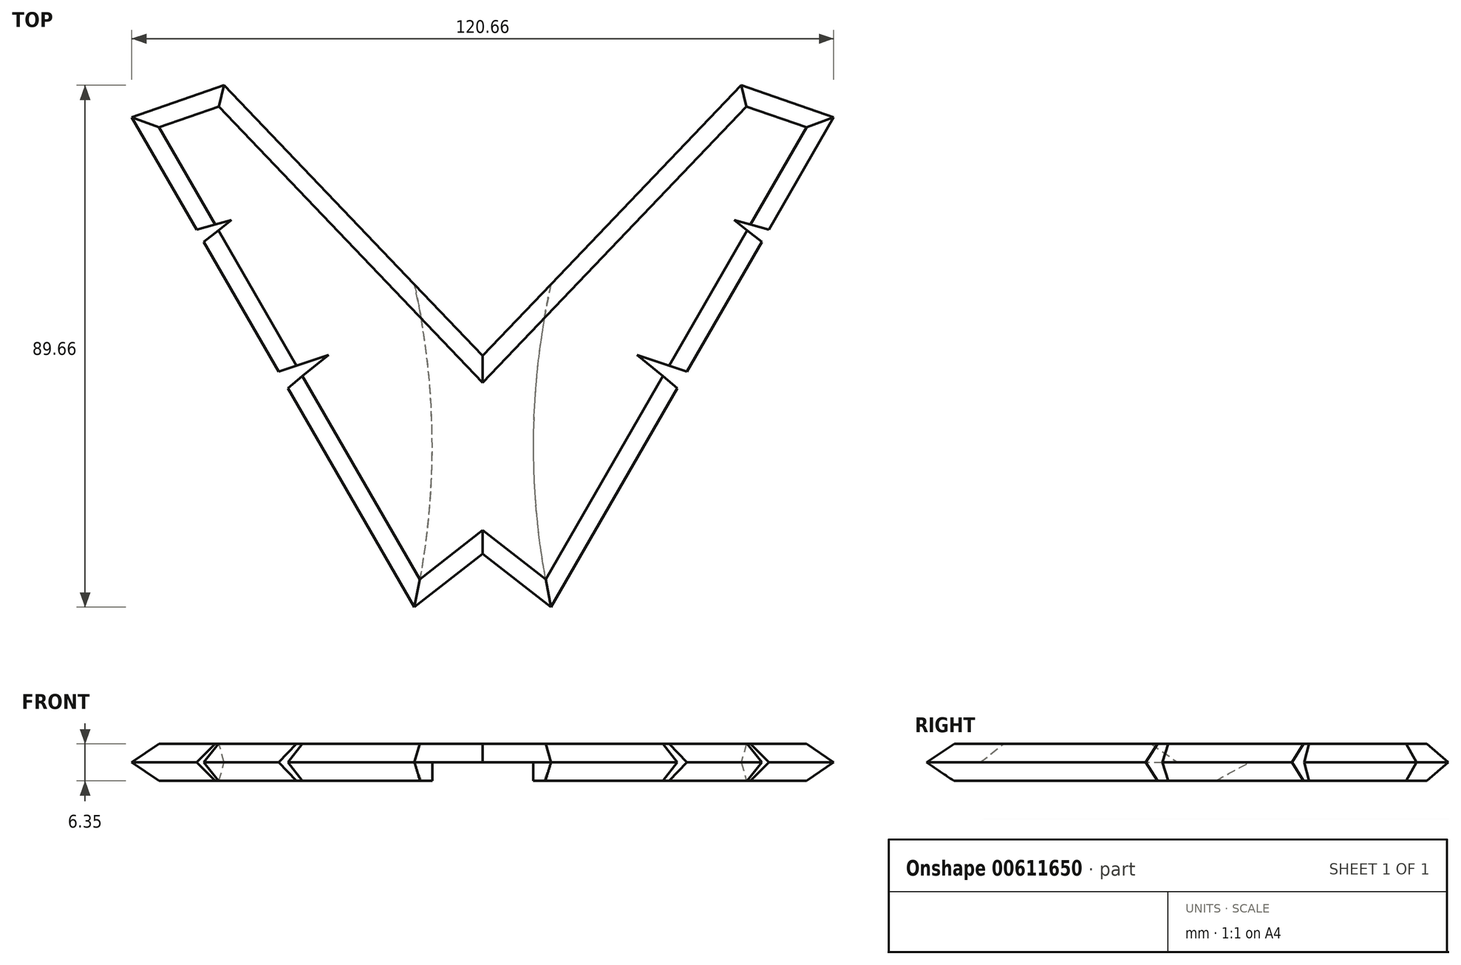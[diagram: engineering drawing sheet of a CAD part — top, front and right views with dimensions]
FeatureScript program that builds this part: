
annotation { "Feature Type Name" : "Feature", "Feature Type Description" : "" }
export const myFeature = defineFeature(function(context is Context, id is Id, definition is map)
    precondition{}
    {
        {
            var Q0;
            Q0=qCreatedBy(makeId("Top.planeOp"),FACE);
            var sketch = newSketch(context, id + "F0", { "sketchPlane" : qUnion([Q0])});
            skLineSegment(sketch, "E0", {"start": v(0, 0) * mm, "end": v(-11.74, 20.33) * mm});
            skLineSegment(sketch, "E1", {"start": v(-63.5, 109.99) * mm, "end": v(63.5, 109.99) * mm});
            skLineSegment(sketch, "E2", {"start": v(63.5, 109.99) * mm, "end": v(0, 0) * mm});
            skLineSegment(sketch, "E3", {"start": v(0, 0) * mm, "end": v(0, 19.44) * mm});
            skLineSegment(sketch, "E4", {"start": v(-60.33, 104.49) * mm, "end": v(-44.45, 109.99) * mm});
            skLineSegment(sketch, "E5.MirrorCS", {"start": v(60.33, 104.49) * mm, "end": v(44.45, 109.99) * mm});
            skLineSegment(sketch, "E6", {"start": v(-44.45, 109.99) * mm, "end": v(0, 63.5) * mm});
            skLineSegment(sketch, "E7", {"start": v(0, 63.5) * mm, "end": v(44.45, 109.99) * mm});
            skPoint(sketch, "E8", {"position": v(-11.74, 20.33) * mm});
            skPoint(sketch, "E9.MirrorP", {"position": v(11.74, 20.33) * mm});
            skLineSegment(sketch, "E10.MirrorCS", {"start": v(11.74, 20.33) * mm, "end": v(0, 29.52) * mm});
            skLineSegment(sketch, "E11.MirrorCS", {"start": v(0, 29.52) * mm, "end": v(-11.74, 20.33) * mm});
            skLineSegment(sketch, "E12", {"start": v(-49.19, 85.2) * mm, "end": v(-43.22, 86.8) * mm});
            skLineSegment(sketch, "E13", {"start": v(-43.22, 86.8) * mm, "end": v(-47.97, 83.1) * mm});
            skLineSegment(sketch, "E14", {"start": v(-35.1, 60.8) * mm, "end": v(-26.52, 63.68) * mm});
            skLineSegment(sketch, "E15", {"start": v(-26.52, 63.68) * mm, "end": v(-33.47, 57.97) * mm});
            skLineSegment(sketch, "E16.trimOffspring", {"start": v(-21.1, 36.55) * mm, "end": v(-33.47, 57.97) * mm});
            skLineSegment(sketch, "E17.trimOffspring", {"start": v(-35.1, 60.8) * mm, "end": v(-47.97, 83.1) * mm});
            skLineSegment(sketch, "E18.trimOffspring", {"start": v(-49.19, 85.2) * mm, "end": v(-63.5, 109.99) * mm});
            skLineSegment(sketch, "E19.MirrorCS", {"start": v(26.52, 63.68) * mm, "end": v(33.47, 57.97) * mm});
            skLineSegment(sketch, "E20.MirrorCS", {"start": v(35.1, 60.8) * mm, "end": v(26.52, 63.68) * mm});
            skLineSegment(sketch, "E21.MirrorCS", {"start": v(43.22, 86.8) * mm, "end": v(47.97, 83.1) * mm});
            skLineSegment(sketch, "E22.MirrorCS", {"start": v(49.19, 85.2) * mm, "end": v(43.22, 86.8) * mm});
            skLineSegment(sketch, "E23", {"start": v(-21.1, 36.55) * mm, "end": v(-11.74, 20.33) * mm});
            skSolve(sketch);
        }
        {
            var Q0;
            {var subQ3=sQuery(id+"F0.wireOp",EDGE,"E4");Q0=makeQuery(id+"F0.imprint","IMPRINT",FACE,{"disambiguationData":[TD([[makeQuery(id+"F0.imprint","IMPRINT",EDGE,{"derivedFrom":subQ3}),-1.0]])]});}
            extrude(context, id + "F1", {"entities" : qUnion([Q0]), "depth" : 6.35 * mm, "offsetDistance" : 25.4 * mm});
        }
        {
            var Q0;
            Q0=makeQuery(id+"F1.opExtrude","CAP_FACE",FACE,{"disambiguationData":[OSD([sQuery(id+"F0.wireOp",EDGE,"E2"),sQuery(id+"F0.wireOp",EDGE,"E4"),sQuery(id+"F0.wireOp",EDGE,"E5.MirrorCS"),sQuery(id+"F0.wireOp",EDGE,"E6"),sQuery(id+"F0.wireOp",EDGE,"E7"),sQuery(id+"F0.wireOp",EDGE,"E10.MirrorCS"),sQuery(id+"F0.wireOp",EDGE,"E11.MirrorCS"),sQuery(id+"F0.wireOp",EDGE,"E12"),sQuery(id+"F0.wireOp",EDGE,"E13"),sQuery(id+"F0.wireOp",EDGE,"E14"),sQuery(id+"F0.wireOp",EDGE,"E15"),sQuery(id+"F0.wireOp",EDGE,"E16.trimOffspring"),sQuery(id+"F0.wireOp",EDGE,"E17.trimOffspring"),sQuery(id+"F0.wireOp",EDGE,"E18.trimOffspring"),sQuery(id+"F0.wireOp",EDGE,"E19.MirrorCS"),sQuery(id+"F0.wireOp",EDGE,"E20.MirrorCS"),sQuery(id+"F0.wireOp",EDGE,"E21.MirrorCS"),sQuery(id+"F0.wireOp",EDGE,"E22.MirrorCS"),sQuery(id+"F0.wireOp",EDGE,"E23")])],"isStart":true});
            var sketch = newSketch(context, id + "F2", { "sketchPlane" : qUnion([Q0])});
            skPoint(sketch, "E24", {"position": v(11.74, -75.77) * mm});
            skPoint(sketch, "E25", {"position": v(-11.74, -75.77) * mm});
            skArc(sketch, "E26", {"start": v(11.74, -20.33) * mm, "mid": v(8.67, -48.05) * mm, "end": v(11.74, -75.77) * mm});
            skArc(sketch, "E27.MirrorCS", {"start": v(-11.74, -20.33) * mm, "mid": v(-8.67, -48.05) * mm, "end": v(-11.74, -75.77) * mm});
            skLineSegment(sketch, "E28", {"start": v(11.74, -75.77) * mm, "end": v(-11.74, -75.77) * mm});
            skLineSegment(sketch, "E29", {"start": v(-11.74, -20.33) * mm, "end": v(11.74, -20.33) * mm});
            skSolve(sketch);
        }
        {
            var Q0;
            {var subQ5=sQuery(id+"F2.wireOp",EDGE,"E26");Q0=makeQuery(id+"F2.imprint","IMPRINT",FACE,{"disambiguationData":[TD([[makeQuery(id+"F2.imprint","IMPRINT",EDGE,{"derivedFrom":subQ5}),-1.0]])]});}
            var Q1;
            {var subQ0=sQuery(id+"F2.wireOp",EDGE,"E28");Q1=makeQuery(id+"F2.imprint","IMPRINT",FACE,{"disambiguationData":[TD([[makeQuery(id+"F2.imprint","IMPRINT",EDGE,{"derivedFrom":subQ0}),-1.0]])]});}
            var Q2;
            Q2=makeQuery(id+"F2.imprint","IMPRINT",FACE,{"disambiguationData":[TD([[makeQuery(id+"F2.imprint","IMPRINT",EDGE,{"derivedFrom":sQuery(id+"F2.wireOp",EDGE,"E29")}),-1.0]])]});
            extrude(context, id + "F3", {"entities" : qUnion([Q0, Q1, Q2]), "operationType" : NewBodyOperationType.REMOVE, "oppositeDirection" : true, "depth" : 3.17 * mm, "offsetDistance" : 25.4 * mm});
        }
        {
            var Q0;
            {var subQ0=sQuery(id+"F0.wireOp",EDGE,"E2");Q0=makeQuery(id+"F1.opExtrude","CAP_EDGE",EDGE,{"disambiguationData":[OSD([subQ0]),TDD([makeQuery(id+"F0.imprint","IMPRINT",EDGE,{"disambiguationData":[TD([[makeQuery(id+"F0.imprint","INTERSECT",VERTEX,{"derivedFrom":[subQ0,sQuery(id+"F0.wireOp",EDGE,"E10.MirrorCS")]}),1.0]])],"derivedFrom":subQ0})])],"isStart":false});}
            var Q1;
            {var subQ0=sQuery(id+"F0.wireOp",EDGE,"E2");Q1=makeQuery(id+"F1.opExtrude","CAP_EDGE",EDGE,{"disambiguationData":[OSD([subQ0]),TDD([makeQuery(id+"F0.imprint","IMPRINT",EDGE,{"disambiguationData":[TD([[makeQuery(id+"F0.imprint","INTERSECT",VERTEX,{"derivedFrom":[subQ0,sQuery(id+"F0.wireOp",EDGE,"E10.MirrorCS")]}),1.0]])],"derivedFrom":subQ0})])],"isStart":true});}
            var Q2;
            {var subQ0=sQuery(id+"F0.wireOp",EDGE,"E2");Q2=makeQuery(id+"F1.opExtrude","CAP_EDGE",EDGE,{"disambiguationData":[OSD([subQ0]),TDD([makeQuery(id+"F0.imprint","IMPRINT",EDGE,{"disambiguationData":[TD([[makeQuery(id+"F0.imprint","INTERSECT",VERTEX,{"derivedFrom":[subQ0,sQuery(id+"F0.wireOp",EDGE,"E20.MirrorCS")]}),1.0]])],"derivedFrom":subQ0})])],"isStart":false});}
            var Q3;
            {var subQ0=sQuery(id+"F0.wireOp",EDGE,"E2");Q3=makeQuery(id+"F1.opExtrude","CAP_EDGE",EDGE,{"disambiguationData":[OSD([subQ0]),TDD([makeQuery(id+"F0.imprint","IMPRINT",EDGE,{"disambiguationData":[TD([[makeQuery(id+"F0.imprint","INTERSECT",VERTEX,{"derivedFrom":[subQ0,sQuery(id+"F0.wireOp",EDGE,"E20.MirrorCS")]}),1.0]])],"derivedFrom":subQ0})])],"isStart":true});}
            var Q4;
            {var subQ0=sQuery(id+"F0.wireOp",EDGE,"E2");Q4=makeQuery(id+"F1.opExtrude","CAP_EDGE",EDGE,{"disambiguationData":[OSD([subQ0]),TDD([makeQuery(id+"F0.imprint","IMPRINT",EDGE,{"disambiguationData":[TD([[makeQuery(id+"F0.imprint","INTERSECT",VERTEX,{"derivedFrom":[subQ0,sQuery(id+"F0.wireOp",EDGE,"E5.MirrorCS")]}),-1.0]])],"derivedFrom":subQ0})])],"isStart":false});}
            var Q5;
            {var subQ0=sQuery(id+"F0.wireOp",EDGE,"E2");Q5=makeQuery(id+"F1.opExtrude","CAP_EDGE",EDGE,{"disambiguationData":[OSD([subQ0]),TDD([makeQuery(id+"F0.imprint","IMPRINT",EDGE,{"disambiguationData":[TD([[makeQuery(id+"F0.imprint","INTERSECT",VERTEX,{"derivedFrom":[subQ0,sQuery(id+"F0.wireOp",EDGE,"E5.MirrorCS")]}),-1.0]])],"derivedFrom":subQ0})])],"isStart":true});}
            var Q6;
            Q6=makeQuery(id+"F1.opExtrude","CAP_EDGE",EDGE,{"disambiguationData":[OSD([sQuery(id+"F0.wireOp",EDGE,"E5.MirrorCS")])],"isStart":false});
            var Q7;
            Q7=makeQuery(id+"F1.opExtrude","CAP_EDGE",EDGE,{"disambiguationData":[OSD([sQuery(id+"F0.wireOp",EDGE,"E5.MirrorCS")])],"isStart":true});
            var Q8;
            Q8=makeQuery(id+"F1.opExtrude","CAP_EDGE",EDGE,{"disambiguationData":[OSD([sQuery(id+"F0.wireOp",EDGE,"E7")])],"isStart":false});
            var Q9;
            Q9=makeQuery(id+"F1.opExtrude","CAP_EDGE",EDGE,{"disambiguationData":[OSD([sQuery(id+"F0.wireOp",EDGE,"E7")])],"isStart":true});
            var Q10;
            Q10=makeQuery(id+"F1.opExtrude","CAP_EDGE",EDGE,{"disambiguationData":[OSD([sQuery(id+"F0.wireOp",EDGE,"E10.MirrorCS")])],"isStart":false});
            var Q11;
            Q11=makeQuery(id+"F1.opExtrude","CAP_EDGE",EDGE,{"disambiguationData":[OSD([sQuery(id+"F0.wireOp",EDGE,"E11.MirrorCS")])],"isStart":false});
            var Q12;
            Q12=makeQuery(id+"F1.opExtrude","CAP_EDGE",EDGE,{"disambiguationData":[OSD([sQuery(id+"F0.wireOp",EDGE,"E6")])],"isStart":false});
            var Q13;
            Q13=makeQuery(id+"F1.opExtrude","CAP_EDGE",EDGE,{"disambiguationData":[OSD([sQuery(id+"F0.wireOp",EDGE,"E6")])],"isStart":true});
            var Q14;
            Q14=makeQuery(id+"F1.opExtrude","CAP_EDGE",EDGE,{"disambiguationData":[OSD([sQuery(id+"F0.wireOp",EDGE,"E4")])],"isStart":false});
            var Q15;
            Q15=makeQuery(id+"F1.opExtrude","CAP_EDGE",EDGE,{"disambiguationData":[OSD([sQuery(id+"F0.wireOp",EDGE,"E4")])],"isStart":true});
            var Q16;
            Q16=makeQuery(id+"F1.opExtrude","CAP_EDGE",EDGE,{"disambiguationData":[OSD([sQuery(id+"F0.wireOp",EDGE,"E18.trimOffspring")])],"isStart":false});
            var Q17;
            Q17=makeQuery(id+"F1.opExtrude","CAP_EDGE",EDGE,{"disambiguationData":[OSD([sQuery(id+"F0.wireOp",EDGE,"E18.trimOffspring")])],"isStart":true});
            var Q18;
            Q18=makeQuery(id+"F1.opExtrude","CAP_EDGE",EDGE,{"disambiguationData":[OSD([sQuery(id+"F0.wireOp",EDGE,"E17.trimOffspring")])],"isStart":false});
            var Q19;
            Q19=makeQuery(id+"F1.opExtrude","CAP_EDGE",EDGE,{"disambiguationData":[OSD([sQuery(id+"F0.wireOp",EDGE,"E17.trimOffspring")])],"isStart":true});
            var Q20;
            Q20=makeQuery(id+"F1.opExtrude","CAP_EDGE",EDGE,{"disambiguationData":[OSD([sQuery(id+"F0.wireOp",EDGE,"E16.trimOffspring"),sQuery(id+"F0.wireOp",EDGE,"E23")])],"isStart":false});
            var Q21;
            Q21=makeQuery(id+"F1.opExtrude","CAP_EDGE",EDGE,{"disambiguationData":[OSD([sQuery(id+"F0.wireOp",EDGE,"E16.trimOffspring"),sQuery(id+"F0.wireOp",EDGE,"E23")])],"isStart":true});
            chamfer(context, id + "F4", {"entities" : qUnion([Q0, Q1, Q2, Q3, Q4, Q5, Q6, Q7, Q8, Q9, Q10, Q11, Q12, Q13, Q14, Q15, Q16, Q17, Q18, Q19, Q20, Q21]), "width" : 3.17 * mm, "tangentPropagation" : true});
        }
    });
